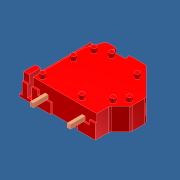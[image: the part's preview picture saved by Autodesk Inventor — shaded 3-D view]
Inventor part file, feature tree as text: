
AUTODESK INVENTOR PART (.ipt)
format: ipt  version: 2012 (Build 160160000, 160)  size: 251,904 bytes
history: native  units: mm (DEFAULTED — no unit token found)
features: sketch x21, extrude x18, revolve x2, pattern_linear x1
ambient origin geometry x8: Origin, YZ Plane, XZ Plane, XY Plane, X Axis, Y Axis, Z Axis, Center Point
bodies: Solid1 (feature_tree)
feature tree (42):
  extrude  "Extrusion1"  Depth=7.5mm TaperAngle=0.0deg
  extrude  "Extrusion2"  Depth=6.6mm TaperAngle=0.0deg
  extrude  "Extrusion3"  Depth=6.3mm TaperAngle=0.0deg
  extrude  "Extrusion4"  Depth=1.5mm TaperAngle=0.0deg
  extrude  "Extrusion5"  Depth=1.5mm TaperAngle=0.0deg
  extrude  "Extrusion6"  Depth=1.5mm TaperAngle=0.0deg
  extrude  "Extrusion7"  Depth=1.5mm TaperAngle=0.0deg
  extrude  "Extrusion8"  Depth=0.5mm TaperAngle=0.0deg
  extrude  "Extrusion9"  Depth=20.0mm TaperAngle=0.0deg
  extrude  "Extrusion10"  TaperAngle=360.0deg  [1 undecoded]
  extrude  "Extrusion11"  [1 undecoded]
  extrude  "Extrusion12"  [1 undecoded]
  extrude  "Extrusion13"  [1 undecoded]
  extrude  "Extrusion14"  [1 undecoded]
  extrude  "Extrusion15"  [1 undecoded]
  extrude  "Extrusion16"  [1 undecoded]
  extrude  "Extrusion17"  [1 undecoded]
  pattern_linear  "Rectangular Pattern1"  [2 undecoded]
  revolve  "Revolution1"  [1 undecoded]
  revolve  "Revolution2"  [1 undecoded]
  extrude  "Extrusion18"  [1 undecoded]
  sketch  "Sketch21"
  sketch  "Skizze_1"  dims[d0=7.5mm d1=0.0mm d2=7.5mm d3=0.0mm]
  sketch  "Skizze_2"  dims[d4=0.8mm d5=0.0mm d6=6.6mm d7=0.0mm]
  sketch  "Skizze_3"  dims[d8=2.8mm d9=0.0mm d10=6.3mm d11=0.0mm]
  sketch  "Skizze_4"  dims[d12=1.5mm d13=0.0mm d14=1.5mm d15=0.0mm]
  sketch  "Skizze_5"  dims[d16=1.5mm d17=0.0mm d18=1.5mm d19=0.0mm]
  sketch  "Skizze_7"  dims[d24=1.5mm d25=0.0mm d26=1.5mm d27=0.0mm]
  sketch  "Skizze_8"  dims[d28=3.5mm d29=0.0mm d30=0.5mm d31=0.0mm]
  sketch  "Skizze_9"  dims[d32=9.0mm d33=0.0mm d34=20.0mm d36=12.5mm d37=10.0mm d39=0.0mm]
  sketch  "Skizze_10"  dims[d40=360.0deg d41=360.0deg]
  sketch  "Skizze_11"  dims[d42=5.8mm d43=0.0mm]
  sketch  "Skizze_12"
  sketch  "Skizze_13"
  sketch  "Skizze_14"
  sketch  "Skizze_15"
  sketch  "Skizze_6"  dims[d20=1.5mm d21=0.0mm d22=1.5mm d23=0.0mm]
  sketch  "Skizze_16"
  sketch  "Skizze_17"
  sketch  "Skizze_19"
  sketch  "Skizze_20"
  sketch  "Skizze_21"
note: 13 required parameter values undecoded (feature->parameter linkage not recoverable at this tier; creation-order binding heuristic only, values carry confidence <= 0.55)
